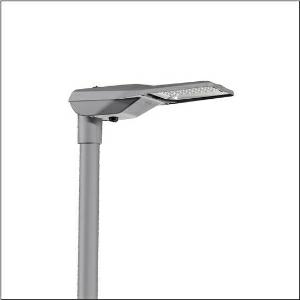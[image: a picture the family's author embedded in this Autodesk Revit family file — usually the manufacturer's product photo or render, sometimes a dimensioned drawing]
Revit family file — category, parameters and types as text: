
# Revit family: streetlight_sl_21_iq_mini___stw1_0a_5xe2e31y08jb_3a8f
name_source: partatom
category: Lighting Fixtures
units: mm (PartAtom-declared; Revit-internal decimal feet)

## family parameters
Cut with Voids When Loaded = No
Host = Face
Light Source = No
Part Type = Normal
Room Calculation Point = No
Round Connector Dimension = Use Diameter
Shared = No

## types (1)
- --- (1 x LED, 11210 lm, 72.5 W, 3000K)
    Apparent Load = 73 VA
    CIE Flux Codes = 39 75 98 100 100
    Color Rendering = 70
    Color Temperature = 3000K
    Default Elevation = 1800 mm
    Description = Streetlight SL 21 iQ mini, mast luminaire, primary light control with lens, of PMMA, primary optical cover: cover, of toughened safety glass, transparent, light distribution: STW1.0a, light emission: direct distribution, primary light characteristic: asymmetric, installation type: post-top, side-entry, LED, High Power LED, rated luminous flux: 11.210lm, luminous efficacy: 155lm/W, light colour: 730, colour temperature: 3000K, control gear: iQ-Street Remote, D4i with power reduction, control: pre-setting: logarithmic dimming characteristic, Street-Remote, Auto-Match, Temp-Guard, Lumen-Switch, Night-Set, Smart-Wire, Light-Fading, Desk-Remote (wireless, voltage-free reading and setting of iQ features in the workshop via application-optimized NFC function/RFID function), optimised constant luminous flux control (CLO 2.0), mains connection: 220..240V, AC, 50/60Hz, start of lifetime: 73W, end of service life: 76W, reduction: 33W, luminaire housing, of diecast aluminium, powder-coated, SITECO metallic grey (DB 702S), corrosivity category C5 high according to DIN EN ISO 12944, please order mast flange separately, inclination adjustable: 0°, 5°, 10°, 15°, sealing non-destructively replaceable, multi-level sealing system, length: 628mm, width: 235mm, height: 110mm, mast flange for spigot size: 42mm (side-entry): 5XC10008XM4, 60/48mm (side-entry/post-top): 5XC10108XM2, 76/60mm (side-entry/post-top): 5XC10108XM1, mounting height: 4..8m, Smart Interface below and above, protection rating (complete): IP66, insulation class (complete): insulation class II (safety insulation), certification: CE, ENEC, ENEC+, VDE, impact resistance: IK10, permissible operating ambient temperature for outdoor applications: -40..+50°C, standard-compliant lighting for roads and squares, packaging unit: 1 piece

Light Distribution: STW1.0a
    Height = 110 mm
    Lamp = 1 x LED
    Lamp Light Flux = 11210 lm
    Lamp Power = 72.5 W
    Lamp count = 1
    Length = 625 mm
    Luminous efficacy = 155 lm/W
    Manufacturer = Siteco
    ModVariant = No
    Model = 5XE2E31Y08JB
    Number of Poles = 1
    OnlyDefault = Yes
    Power Factor = 1
    Product Name = Streetlight SL 21 iQ mini | STW1.0a
    Product group = mast luminaire | pylon top
    ProductGroupID = 6100
    Protection Class = Protection class II
    Protection Degree = IP 66
    RLX_Detail_Level = 1
    RLX_Emergency_Light_Flux = 0 lm
    RLX_Emergency_Type = 0
    RLX_Emergency_Type_DB = No
    RlxData = <blob elided: 92913 chars, md5=0c3f9a87>
    Socket = socket
    Standby Power = 0 W
    System Light Flux = 11210 lm
    System Power = 73 W
    Type Comments = factory setting: luminous flux: 100 % | dim-lin: 254 | 755 mA
    Type Image = l_1003514.jpg
    URL = http://relux.com
    VarID = @adj_113815
    Voltage = 0 V
    Weight = 0.00 kg
    Width = 234 mm

## geometry (parser evidence)
native form markers: Blend x4, Sweep x11
no freeform markers — native parametric forms only
